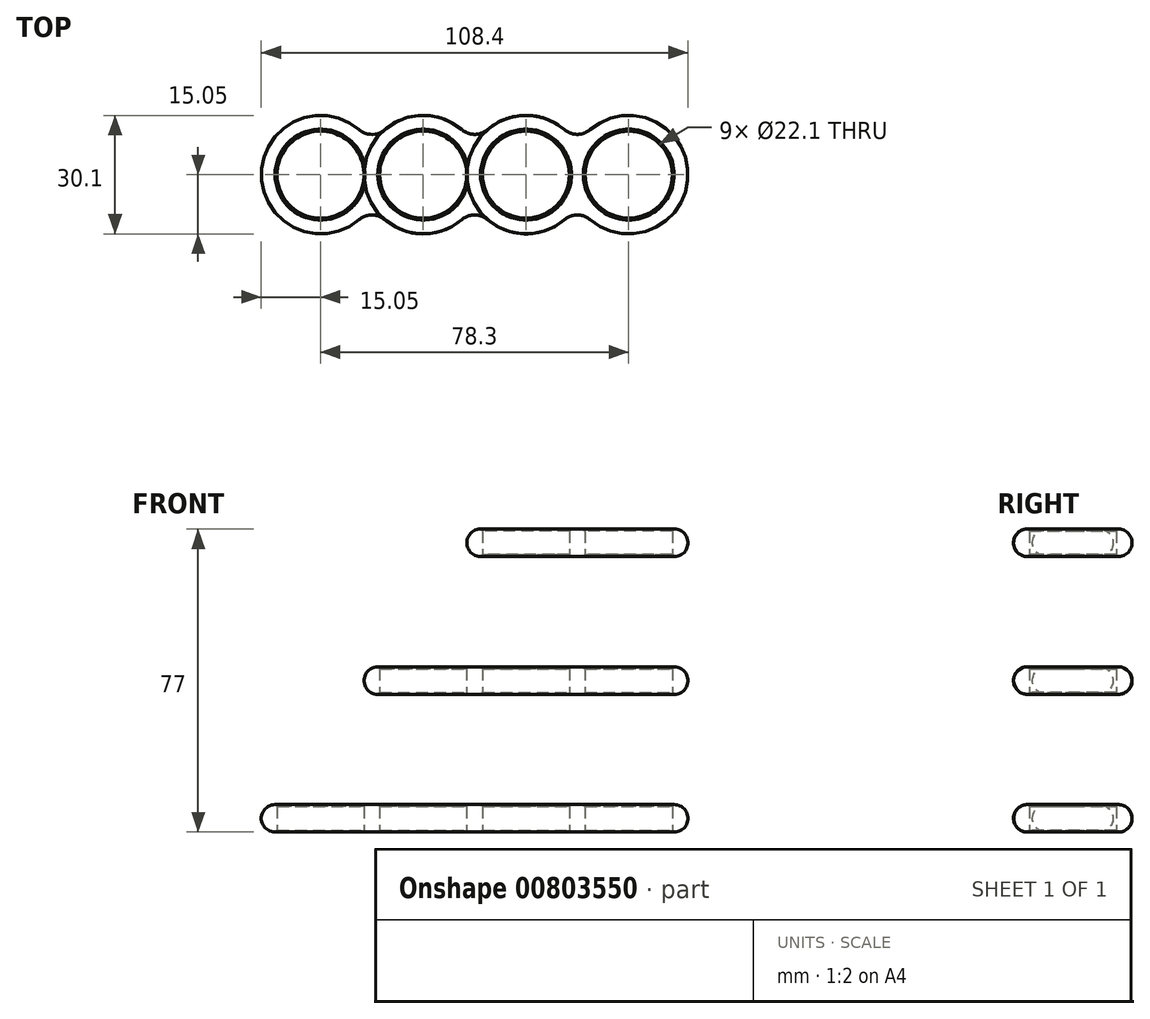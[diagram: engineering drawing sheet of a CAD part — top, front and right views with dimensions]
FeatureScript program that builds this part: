
annotation { "Feature Type Name" : "Feature", "Feature Type Description" : "" }
export const myFeature = defineFeature(function(context is Context, id is Id, definition is map)
    precondition{}
    {
        {
            var Q0;
            Q0=qCreatedBy(makeId("Top.planeOp"),FACE);
            var sketch = newSketch(context, id + "F0", { "sketchPlane" : qUnion([Q0])});
            skCircle(sketch, "E0", {"center": v(-13.05, 0) * mm, "radius": 11.05 * mm});
            skCircle(sketch, "E1", {"center": v(13.05, 0) * mm, "radius": 11.05 * mm});
            skArc(sketch, "E2", {"start": v(-3.25, 11.43) * mm, "mid": v(-28.1, 0) * mm, "end": v(-3.25, -11.43) * mm});
            skArc(sketch, "E3", {"start": v(3.25, -11.43) * mm, "mid": v(28.1, 0) * mm, "end": v(3.25, 11.43) * mm});
            skLineSegment(sketch, "E4", {"start": v(-13.05, 0) * mm, "end": v(13.05, 0) * mm, "construction": true});
            skPoint(sketch, "E5.visualSharp", {"position": v(0, 7.5) * mm});
            skArc(sketch, "E5.filletArc", {"start": v(-3.25, 11.43) * mm, "mid": v(0, 10.22) * mm, "end": v(3.25, 11.43) * mm});
            skPoint(sketch, "E6.visualSharp", {"position": v(0, -7.5) * mm});
            skArc(sketch, "E6.filletArc", {"start": v(3.25, -11.43) * mm, "mid": v(0, -10.22) * mm, "end": v(-3.25, -11.43) * mm});
            skSolve(sketch);
        }
        {
            var Q0;
            Q0=makeQuery(id+"F0.imprint","IMPRINT",FACE,{"disambiguationData":[TD([[makeQuery(id+"F0.imprint","IMPRINT",EDGE,{"derivedFrom":sQuery(id+"F0.wireOp",EDGE,"E0")}),-1.0]])]});
            extrude(context, id + "F1", {"entities" : qUnion([Q0]), "depth" : 7 * mm, "offsetDistance" : 25 * mm});
        }
        {
            var Q0;
            Q0=makeQuery(id+"F1.opExtrude","CAP_EDGE",EDGE,{"disambiguationData":[OSD([sQuery(id+"F0.wireOp",EDGE,"E2")])],"isStart":false});
            var Q1;
            Q1=makeQuery(id+"F1.opExtrude","CAP_EDGE",EDGE,{"disambiguationData":[OSD([sQuery(id+"F0.wireOp",EDGE,"E2")])],"isStart":true});
            fillet(context, id + "F2", {"entities" : qUnion([Q0, Q1]), "radius" : 3.5 * mm, "tangentPropagation" : true, "allowEdgeOverflow" : false});
        }
        {
            var Q0;
            Q0=makeQuery(id+"F1.opExtrude","SWEPT_FACE",FACE,{"disambiguationData":[OSD([sQuery(id+"F0.wireOp",EDGE,"E0")])]});
            var Q1;
            Q1=makeQuery(id+"F1.opExtrude","SWEPT_FACE",FACE,{"disambiguationData":[OSD([sQuery(id+"F0.wireOp",EDGE,"E1")])]});
            chamfer(context, id + "F3", {"entities" : qUnion([Q0, Q1]), "width" : .5 * mm, "tangentPropagation" : true});
        }
        {
            var Q0;
            Q0=makeQuery(id+"F1.opExtrude","CAP_FACE",FACE,{"disambiguationData":[OSD([sQuery(id+"F0.wireOp",EDGE,"E0"),sQuery(id+"F0.wireOp",EDGE,"E1"),sQuery(id+"F0.wireOp",EDGE,"E2"),sQuery(id+"F0.wireOp",EDGE,"E3"),sQuery(id+"F0.wireOp",EDGE,"E5.filletArc"),sQuery(id+"F0.wireOp",EDGE,"E6.filletArc")])],"isStart":true});
            cPlane(context, id + "F4", {"entities" : qUnion([Q0]), "cplaneType" : CPlaneType.OFFSET, "offset" : 35 * mm, "width" : 150 * mm, "height" : 150 * mm});
        }
        {
            var Q0;
            Q0=qCreatedBy(id+"F4.planeOp",FACE);
            var sketch = newSketch(context, id + "F5", { "sketchPlane" : qUnion([Q0])});
            skCircle(sketch, "E7", {"center": v(-13.05, 0) * mm, "radius": 11.05 * mm});
            skCircle(sketch, "E8", {"center": v(13.05, 0) * mm, "radius": 11.05 * mm});
            skCircle(sketch, "E9", {"center": v(-39.15, 0) * mm, "radius": 11.05 * mm});
            skLineSegment(sketch, "E10", {"start": v(-39.15, 0) * mm, "end": v(-13.05, 0) * mm, "construction": true});
            skLineSegment(sketch, "E11", {"start": v(-13.05, 0) * mm, "end": v(13.05, 0) * mm, "construction": true});
            skArc(sketch, "E12", {"start": v(-29.35, 11.43) * mm, "mid": v(-54.2, 0) * mm, "end": v(-29.35, -11.43) * mm});
            skArc(sketch, "E13", {"start": v(-22.85, -11.43) * mm, "mid": v(-13.05, -15.05) * mm, "end": v(-3.25, -11.43) * mm});
            skArc(sketch, "E14", {"start": v(3.25, -11.43) * mm, "mid": v(28.1, 0) * mm, "end": v(3.25, 11.43) * mm});
            skArc(sketch, "E15.trimOffspring", {"start": v(-3.25, 11.43) * mm, "mid": v(-13.05, 15.05) * mm, "end": v(-22.85, 11.43) * mm});
            skPoint(sketch, "E16.visualSharp", {"position": v(-26.1, 7.5) * mm});
            skArc(sketch, "E16.filletArc", {"start": v(-29.35, 11.43) * mm, "mid": v(-26.1, 10.22) * mm, "end": v(-22.85, 11.43) * mm});
            skPoint(sketch, "E17.visualSharp", {"position": v(0, 7.5) * mm});
            skArc(sketch, "E17.filletArc", {"start": v(-3.25, 11.43) * mm, "mid": v(0, 10.22) * mm, "end": v(3.25, 11.43) * mm});
            skPoint(sketch, "E18.visualSharp", {"position": v(0, -7.5) * mm});
            skArc(sketch, "E18.filletArc", {"start": v(3.25, -11.43) * mm, "mid": v(0, -10.22) * mm, "end": v(-3.25, -11.43) * mm});
            skPoint(sketch, "E19.visualSharp", {"position": v(-26.1, -7.5) * mm});
            skArc(sketch, "E19.filletArc", {"start": v(-22.85, -11.43) * mm, "mid": v(-26.1, -10.22) * mm, "end": v(-29.35, -11.43) * mm});
            skSolve(sketch);
        }
        {
            var Q0;
            Q0=makeQuery(id+"F5.imprint","IMPRINT",FACE,{"disambiguationData":[TD([[makeQuery(id+"F5.imprint","IMPRINT",EDGE,{"derivedFrom":sQuery(id+"F5.wireOp",EDGE,"E7")}),-1.0]])]});
            extrude(context, id + "F6", {"entities" : qUnion([Q0]), "oppositeDirection" : true, "depth" : 7 * mm, "offsetDistance" : 25 * mm});
        }
        {
            var Q0;
            Q0=makeQuery(id+"F6.opExtrude","CAP_EDGE",EDGE,{"disambiguationData":[OSD([sQuery(id+"F5.wireOp",EDGE,"E16.filletArc")])],"isStart":false});
            var Q1;
            Q1=makeQuery(id+"F6.opExtrude","CAP_EDGE",EDGE,{"disambiguationData":[OSD([sQuery(id+"F5.wireOp",EDGE,"E16.filletArc")])],"isStart":true});
            fillet(context, id + "F7", {"entities" : qUnion([Q0, Q1]), "radius" : 3.5 * mm, "tangentPropagation" : true, "allowEdgeOverflow" : false});
        }
        {
            var Q0;
            Q0=makeQuery(id+"F6.opExtrude","SWEPT_FACE",FACE,{"disambiguationData":[OSD([sQuery(id+"F5.wireOp",EDGE,"E9")])]});
            var Q1;
            Q1=makeQuery(id+"F6.opExtrude","SWEPT_FACE",FACE,{"disambiguationData":[OSD([sQuery(id+"F5.wireOp",EDGE,"E7")])]});
            var Q2;
            Q2=makeQuery(id+"F6.opExtrude","SWEPT_FACE",FACE,{"disambiguationData":[OSD([sQuery(id+"F5.wireOp",EDGE,"E8")])]});
            chamfer(context, id + "F8", {"entities" : qUnion([Q0, Q1, Q2]), "width" : .5 * mm, "tangentPropagation" : true});
        }
        {
            var Q0;
            Q0=makeQuery(id+"F8.opChamfer","SPLIT",FACE,{"disambiguationData":[OD(1.0)],"derivedFrom":makeQuery(id+"F6.opExtrude","CAP_FACE",FACE,{"disambiguationData":[OSD([sQuery(id+"F5.wireOp",EDGE,"E7"),sQuery(id+"F5.wireOp",EDGE,"E8"),sQuery(id+"F5.wireOp",EDGE,"E9"),sQuery(id+"F5.wireOp",EDGE,"E12"),sQuery(id+"F5.wireOp",EDGE,"E13"),sQuery(id+"F5.wireOp",EDGE,"E14"),sQuery(id+"F5.wireOp",EDGE,"E15.trimOffspring"),sQuery(id+"F5.wireOp",EDGE,"E16.filletArc"),sQuery(id+"F5.wireOp",EDGE,"E17.filletArc"),sQuery(id+"F5.wireOp",EDGE,"E18.filletArc"),sQuery(id+"F5.wireOp",EDGE,"E19.filletArc")])],"isStart":true})});
            cPlane(context, id + "F9", {"entities" : qUnion([Q0]), "cplaneType" : CPlaneType.OFFSET, "offset" : 35 * mm, "width" : 150 * mm, "height" : 150 * mm});
        }
        {
            var Q0;
            Q0=qCreatedBy(id+"F9.planeOp",FACE);
            var sketch = newSketch(context, id + "F10", { "sketchPlane" : qUnion([Q0])});
            skCircle(sketch, "E20", {"center": v(13.05, 0) * mm, "radius": 11.05 * mm});
            skCircle(sketch, "E21", {"center": v(-13.05, 0) * mm, "radius": 11.05 * mm});
            skCircle(sketch, "E22", {"center": v(-39.15, 0) * mm, "radius": 11.05 * mm});
            skCircle(sketch, "E23", {"center": v(-65.25, 0) * mm, "radius": 11.05 * mm});
            skLineSegment(sketch, "E24", {"start": v(-65.25, 0) * mm, "end": v(-39.15, 0) * mm, "construction": true});
            skLineSegment(sketch, "E25", {"start": v(-39.15, 0) * mm, "end": v(-13.05, 0) * mm, "construction": true});
            skLineSegment(sketch, "E26", {"start": v(-13.05, 0) * mm, "end": v(13.05, 0) * mm, "construction": true});
            skArc(sketch, "E27", {"start": v(3.25, -11.43) * mm, "mid": v(28.1, 0) * mm, "end": v(3.25, 11.43) * mm});
            skArc(sketch, "E28", {"start": v(-22.85, -11.43) * mm, "mid": v(-13.05, -15.05) * mm, "end": v(-3.25, -11.43) * mm});
            skArc(sketch, "E29", {"start": v(-48.95, -11.43) * mm, "mid": v(-39.15, -15.05) * mm, "end": v(-29.35, -11.43) * mm});
            skArc(sketch, "E30", {"start": v(-55.45, 11.43) * mm, "mid": v(-80.3, 0) * mm, "end": v(-55.45, -11.43) * mm});
            skArc(sketch, "E31.trimOffspring", {"start": v(-29.35, 11.43) * mm, "mid": v(-39.15, 15.05) * mm, "end": v(-48.95, 11.43) * mm});
            skArc(sketch, "E32.trimOffspring", {"start": v(-3.25, 11.43) * mm, "mid": v(-13.05, 15.05) * mm, "end": v(-22.85, 11.43) * mm});
            skPoint(sketch, "E33.visualSharp", {"position": v(-52.2, 7.5) * mm});
            skArc(sketch, "E33.filletArc", {"start": v(-55.45, 11.43) * mm, "mid": v(-52.2, 10.22) * mm, "end": v(-48.95, 11.43) * mm});
            skPoint(sketch, "E34.visualSharp", {"position": v(-26.1, 7.5) * mm});
            skArc(sketch, "E34.filletArc", {"start": v(-29.35, 11.43) * mm, "mid": v(-26.1, 10.22) * mm, "end": v(-22.85, 11.43) * mm});
            skPoint(sketch, "E35.visualSharp", {"position": v(0, 7.5) * mm});
            skArc(sketch, "E35.filletArc", {"start": v(-3.25, 11.43) * mm, "mid": v(0, 10.22) * mm, "end": v(3.25, 11.43) * mm});
            skPoint(sketch, "E36.visualSharp", {"position": v(0, -7.5) * mm});
            skArc(sketch, "E36.filletArc", {"start": v(3.25, -11.43) * mm, "mid": v(0, -10.22) * mm, "end": v(-3.25, -11.43) * mm});
            skPoint(sketch, "E37.visualSharp", {"position": v(-26.1, -7.5) * mm});
            skArc(sketch, "E37.filletArc", {"start": v(-22.85, -11.43) * mm, "mid": v(-26.1, -10.22) * mm, "end": v(-29.35, -11.43) * mm});
            skPoint(sketch, "E38.visualSharp", {"position": v(-52.2, -7.5) * mm});
            skArc(sketch, "E38.filletArc", {"start": v(-48.95, -11.43) * mm, "mid": v(-52.2, -10.22) * mm, "end": v(-55.45, -11.43) * mm});
            skSolve(sketch);
        }
        {
            var Q0;
            Q0=makeQuery(id+"F10.imprint","IMPRINT",FACE,{"disambiguationData":[TD([[makeQuery(id+"F10.imprint","IMPRINT",EDGE,{"derivedFrom":sQuery(id+"F10.wireOp",EDGE,"E20")}),-1.0]])]});
            extrude(context, id + "F11", {"entities" : qUnion([Q0]), "oppositeDirection" : true, "depth" : 7 * mm, "offsetDistance" : 25 * mm});
        }
        {
            var Q0;
            Q0=makeQuery(id+"F11.opExtrude","CAP_EDGE",EDGE,{"disambiguationData":[OSD([sQuery(id+"F10.wireOp",EDGE,"E33.filletArc")])],"isStart":false});
            var Q1;
            Q1=makeQuery(id+"F11.opExtrude","CAP_EDGE",EDGE,{"disambiguationData":[OSD([sQuery(id+"F10.wireOp",EDGE,"E33.filletArc")])],"isStart":true});
            fillet(context, id + "F12", {"entities" : qUnion([Q0, Q1]), "radius" : 3.5 * mm, "tangentPropagation" : true, "allowEdgeOverflow" : false});
        }
        {
            var Q0;
            Q0=makeQuery(id+"F11.opExtrude","SWEPT_FACE",FACE,{"disambiguationData":[OSD([sQuery(id+"F10.wireOp",EDGE,"E23")])]});
            var Q1;
            Q1=makeQuery(id+"F11.opExtrude","SWEPT_FACE",FACE,{"disambiguationData":[OSD([sQuery(id+"F10.wireOp",EDGE,"E22")])]});
            var Q2;
            Q2=makeQuery(id+"F11.opExtrude","SWEPT_FACE",FACE,{"disambiguationData":[OSD([sQuery(id+"F10.wireOp",EDGE,"E21")])]});
            var Q3;
            Q3=makeQuery(id+"F11.opExtrude","SWEPT_FACE",FACE,{"disambiguationData":[OSD([sQuery(id+"F10.wireOp",EDGE,"E20")])]});
            chamfer(context, id + "F13", {"entities" : qUnion([Q0, Q1, Q2, Q3]), "width" : .5 * mm, "tangentPropagation" : true});
        }
    });
